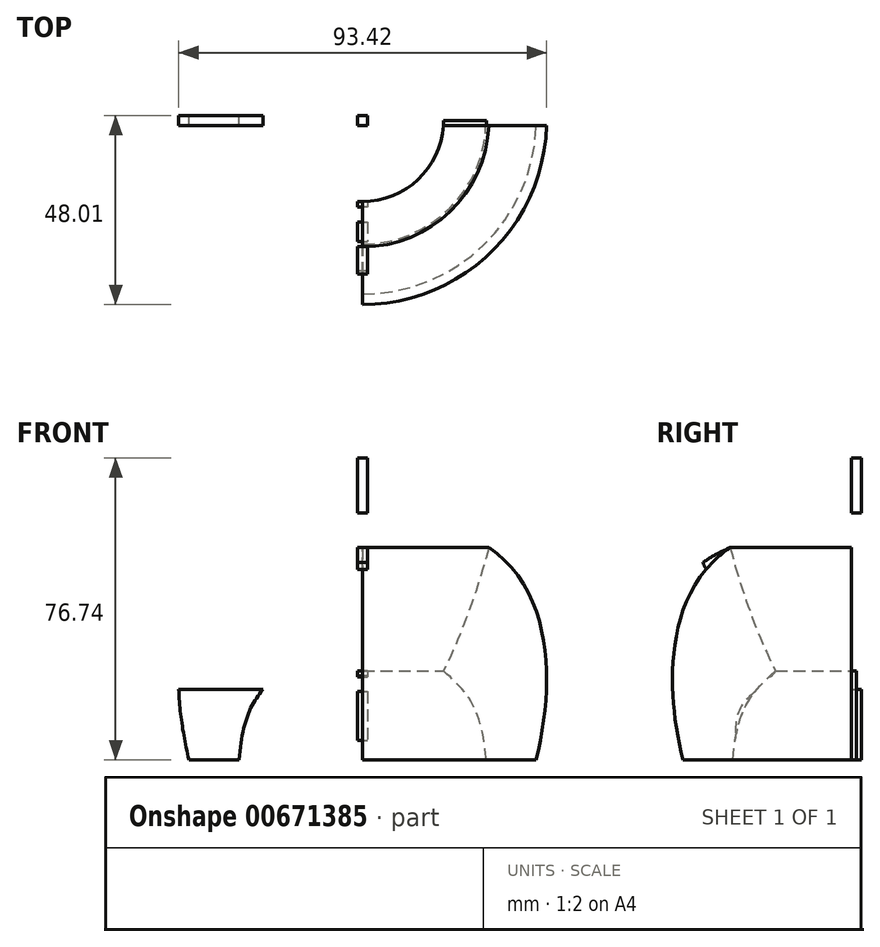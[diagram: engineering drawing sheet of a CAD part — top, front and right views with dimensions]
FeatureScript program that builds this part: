
annotation { "Feature Type Name" : "Feature", "Feature Type Description" : "" }
export const myFeature = defineFeature(function(context is Context, id is Id, definition is map)
    precondition{}
    {
        {
            var Q0;
            Q0=qCreatedBy(makeId("Front.planeOp"),FACE);
            var sketch = newSketch(context, id + "F0", { "sketchPlane" : qUnion([Q0])});
            skLineSegment(sketch, "E0", {"start": v(0, 0) * mm, "end": v(0, 203.2) * mm, "construction": true});
            skFitSpline(sketch, "E1", {"points": [v(0, 203.2) * mm, v(38.56, 109.4) * mm, v(12.7, 9.52) * mm], "startDerivative": vector(125.06, -59.8) * mm, "endDerivative": vector(-79, -104.87) * mm});
            skFitSpline(sketch, "E2.MirrorCS", {"points": [v(0, 203.2) * mm, v(-38.56, 109.4) * mm, v(-12.7, 9.52) * mm], "startDerivative": vector(-125.06, -59.8) * mm, "endDerivative": vector(79, -104.87) * mm});
            skLineSegment(sketch, "E3", {"start": v(-12.7, 9.52) * mm, "end": v(12.7, 9.53) * mm});
            skLineSegment(sketch, "E4", {"start": v(31.41, 0) * mm, "end": v(44.11, 0) * mm});
            skFitSpline(sketch, "E5", {"points": [v(44.11, 0) * mm, v(46.52, 25.68) * mm, v(32.09, 54) * mm], "startDerivative": vector(12.74, 54.23) * mm, "endDerivative": vector(-60.54, 42.84) * mm});
            skFitSpline(sketch, "E6", {"points": [v(31.41, 0) * mm, v(20.56, 22.58) * mm], "startDerivative": vector(-3.27, 36.67) * mm, "endDerivative": vector(-20.85, 17.87) * mm});
            skFitSpline(sketch, "E7.MirrorCS", {"points": [v(-44.11, 0) * mm, v(-46.52, 25.68) * mm, v(-32.09, 54) * mm], "startDerivative": vector(-12.74, 54.23) * mm, "endDerivative": vector(60.54, 42.84) * mm});
            skLineSegment(sketch, "E8.MirrorCS", {"start": v(-31.41, 0) * mm, "end": v(-44.11, 0) * mm});
            skFitSpline(sketch, "E9.MirrorCS", {"points": [v(-31.41, 0) * mm, v(-20.56, 22.58) * mm], "startDerivative": vector(3.27, 36.67) * mm, "endDerivative": vector(20.85, 17.87) * mm});
            skSolve(sketch);
        }
        {
            var Q0;
            {var subQ4=sQuery(id+"F0.wireOp",EDGE,"E3");Q0=makeQuery(id+"F0.imprint","IMPRINT",FACE,{"disambiguationData":[TD([[makeQuery(id+"F0.imprint","IMPRINT",EDGE,{"derivedFrom":subQ4}),1.0]])]});}
            var Q1;
            {var subQ0=sQuery(id+"F0.wireOp",EDGE,"E7.MirrorCS");Q1=makeQuery(id+"F0.imprint","IMPRINT",FACE,{"disambiguationData":[TD([[makeQuery(id+"F0.imprint","IMPRINT",EDGE,{"derivedFrom":subQ0}),-1.0]])]});}
            var Q2;
            Q2=makeQuery(id+"F0.imprint","IMPRINT",FACE,{"disambiguationData":[TD([[makeQuery(id+"F0.imprint","IMPRINT",EDGE,{"derivedFrom":sQuery(id+"F0.wireOp",EDGE,"E4")}),1.0]])]});
            extrude(context, id + "F1", {"entities" : qUnion([Q0, Q1, Q2]), "endBound" : BoundingType.SYMMETRIC, "depth" : 2.54 * mm, "offsetDistance" : 25.4 * mm});
        }
        {
            var Q0;
            Q0=makeQuery(id+"F1.opExtrude","SWEPT_EDGE",EDGE,{"disambiguationData":[OSD([sQuery(id+"F0.wireOp",EDGE,"E1"),sQuery(id+"F0.wireOp",EDGE,"E2.MirrorCS")])]});
            fillet(context, id + "F2", {"entities" : qUnion([Q0]), "radius" : 12.7 * mm, "tangentPropagation" : true, "allowEdgeOverflow" : false});
        }
        {
            var Q0;
            Q0=makeQuery(id+"F0.imprint","IMPRINT",FACE,{"disambiguationData":[TD([[makeQuery(id+"F0.imprint","IMPRINT",EDGE,{"derivedFrom":sQuery(id+"F0.wireOp",EDGE,"E4")}),1.0]])]});
            var Q1;
            Q1=sQuery(id+"F0.wireOp",EDGE,"E0");
            revolve(context, id + "F3", {"entities" : qUnion([Q0]), "axis" : qUnion([Q1]), "revolveType" : RevolveType.ONE_DIRECTION, "oppositeDirection" : true, "angle" : 90 * degree});
        }
        {
            var Q0;
            Q0=makeQuery(id+"F3.opRevolve","CAP_FACE",FACE,{"disambiguationData":[OSD([sQuery(id+"F0.wireOp",EDGE,"E1"),sQuery(id+"F0.wireOp",EDGE,"E4"),sQuery(id+"F0.wireOp",EDGE,"E5"),sQuery(id+"F0.wireOp",EDGE,"E6")])],"isStart":false});
            var sketch = newSketch(context, id + "F4", { "sketchPlane" : qUnion([Q0])});
            skFitSpline(sketch, "E10.0.0", {"points": [v(20.56, 22.58) * mm, v(23.55, 19.29) * mm, v(29.71, 12.74) * mm, v(30.83, 4.2) * mm, v(31.41, 0) * mm]});
            skLineSegment(sketch, "E10.0.1", {"start": v(31.41, 0) * mm, "end": v(44.11, 0) * mm});
            skFitSpline(sketch, "E10.0.2", {"points": [v(44.11, 0) * mm, v(46.12, 8.57) * mm, v(48.46, 25.8) * mm, v(42.7, 46.48) * mm, v(32.09, 54) * mm]});
            skFitSpline(sketch, "E10.0.3", {"points": [v(0, 203.2) * mm, v(20.75, 193.28) * mm, v(53.81, 107.91) * mm, v(25.92, 27.08) * mm, v(12.7, 9.52) * mm]});
            skFitSpline(sketch, "E11.MirrorCS", {"points": [v(-44.11, 0) * mm, v(-46.12, 8.57) * mm, v(-48.46, 25.8) * mm, v(-42.7, 46.48) * mm, v(-32.09, 54) * mm]});
            skLineSegment(sketch, "E12.MirrorCS", {"start": v(-31.41, 0) * mm, "end": v(-44.11, 0) * mm});
            skFitSpline(sketch, "E13.MirrorCS", {"points": [v(-20.56, 22.58) * mm, v(-23.55, 19.29) * mm, v(-29.71, 12.74) * mm, v(-30.83, 4.2) * mm, v(-31.41, 0) * mm]});
            skLineSegment(sketch, "E14", {"start": v(0, 62.78) * mm, "end": v(-20.26, 62.78) * mm, "construction": true});
            skFitSpline(sketch, "E15", {"points": [v(0, 62.78) * mm, v(32.09, 54) * mm], "startDerivative": vector(35.76, 0) * mm, "endDerivative": vector(29.19, -20.66) * mm});
            skLineSegment(sketch, "E16", {"start": v(0, 30.67) * mm, "end": v(-16.56, 30.67) * mm, "construction": true});
            skFitSpline(sketch, "E17", {"points": [v(0, 30.67) * mm, v(20.56, 22.58) * mm], "startDerivative": vector(22.33, 0) * mm, "endDerivative": vector(16.96, -14.53) * mm});
            skFitSpline(sketch, "E18.MirrorCS", {"points": [v(0, 62.78) * mm, v(-32.09, 54) * mm], "startDerivative": vector(-35.76, 0) * mm, "endDerivative": vector(-29.19, -20.66) * mm});
            skFitSpline(sketch, "E19.MirrorCS", {"points": [v(0, 30.67) * mm, v(-20.56, 22.58) * mm], "startDerivative": vector(-22.33, 0) * mm, "endDerivative": vector(-16.96, -14.53) * mm});
            skSolve(sketch);
        }
        {
            var Q0;
            Q0=makeQuery(id+"F4.imprint","IMPRINT",FACE,{"disambiguationData":[TD([[makeQuery(id+"F4.imprint","IMPRINT",EDGE,{"derivedFrom":sQuery(id+"F4.wireOp",EDGE,"E10.0.3")}),-1.0]])]});
            var Q1;
            Q1=makeQuery(id+"F4.imprint","IMPRINT",FACE,{"disambiguationData":[TD([[makeQuery(id+"F4.imprint","IMPRINT",EDGE,{"derivedFrom":sQuery(id+"F4.wireOp",EDGE,"E10.0.0")}),-1.0]])]});
            extrude(context, id + "F5", {"entities" : qUnion([Q0, Q1]), "endBound" : BoundingType.SYMMETRIC, "depth" : 2.54 * mm, "offsetDistance" : 25.4 * mm});
        }
        {
            var Q0;
            Q0=makeQuery(id+"F5.opExtrude","CAP_FACE",FACE,{"disambiguationData":[OSD([sQuery(id+"F4.wireOp",EDGE,"E10.0.0"),sQuery(id+"F4.wireOp",EDGE,"E10.0.1"),sQuery(id+"F4.wireOp",EDGE,"E10.0.2"),sQuery(id+"F4.wireOp",EDGE,"E11.MirrorCS"),sQuery(id+"F4.wireOp",EDGE,"E12.MirrorCS"),sQuery(id+"F4.wireOp",EDGE,"E13.MirrorCS"),sQuery(id+"F4.wireOp",EDGE,"E15"),sQuery(id+"F4.wireOp",EDGE,"E17"),sQuery(id+"F4.wireOp",EDGE,"E18.MirrorCS"),sQuery(id+"F4.wireOp",EDGE,"E19.MirrorCS")])],"isStart":true});
            var sketch = newSketch(context, id + "F6", { "sketchPlane" : qUnion([Q0])});
            skLineSegment(sketch, "E20.bottom", {"start": v(1.27, 43.37) * mm, "end": v(-1.27, 43.37) * mm});
            skLineSegment(sketch, "E20.top", {"start": v(1.27, 17.97) * mm, "end": v(-1.27, 17.97) * mm});
            skLineSegment(sketch, "E20.left", {"start": v(1.27, 43.37) * mm, "end": v(1.27, 17.97) * mm});
            skLineSegment(sketch, "E20.right", {"start": v(-1.27, 43.37) * mm, "end": v(-1.27, 17.97) * mm});
            skPoint(sketch, "E20.middle", {"position": v(0, 30.67) * mm});
            skSolve(sketch);
        }
        {
            var Q0;
            {var subQ1=sQuery(id+"F6.wireOp",EDGE,"E20.bottom");Q0=makeQuery(id+"F6.imprint","IMPRINT",FACE,{"disambiguationData":[TD([[makeQuery(id+"F6.imprint","IMPRINT",EDGE,{"derivedFrom":subQ1}),1.0]])]});}
            var Q1;
            {var subQ5=sQuery(id+"F6.wireOp",EDGE,"E20.top");Q1=makeQuery(id+"F6.imprint","IMPRINT",FACE,{"disambiguationData":[TD([[makeQuery(id+"F6.imprint","IMPRINT",EDGE,{"derivedFrom":subQ5}),-1.0]])]});}
            extrude(context, id + "F7", {"entities" : qUnion([Q0, Q1]), "operationType" : NewBodyOperationType.REMOVE, "endBound" : BoundingType.THROUGH_ALL, "oppositeDirection" : true, "depth" : 25.4 * mm, "offsetDistance" : 25.4 * mm});
        }
        {
            var Q0;
            Q0=makeQuery(id+"F5.opExtrude","SWEPT_BODY",BODY,{"disambiguationData":[OSD([sQuery(id+"F4.wireOp",EDGE,"E10.0.0"),sQuery(id+"F4.wireOp",EDGE,"E10.0.1"),sQuery(id+"F4.wireOp",EDGE,"E10.0.2"),sQuery(id+"F4.wireOp",EDGE,"E11.MirrorCS"),sQuery(id+"F4.wireOp",EDGE,"E12.MirrorCS"),sQuery(id+"F4.wireOp",EDGE,"E13.MirrorCS"),sQuery(id+"F4.wireOp",EDGE,"E15"),sQuery(id+"F4.wireOp",EDGE,"E17"),sQuery(id+"F4.wireOp",EDGE,"E18.MirrorCS"),sQuery(id+"F4.wireOp",EDGE,"E19.MirrorCS")])]});
            var Q1;
            Q1=makeQuery(id+"F1.opExtrude","SWEPT_BODY",BODY,{"disambiguationData":[OSD([sQuery(id+"F0.wireOp",EDGE,"E1"),sQuery(id+"F0.wireOp",EDGE,"E2.MirrorCS"),sQuery(id+"F0.wireOp",EDGE,"E3"),sQuery(id+"F0.wireOp",EDGE,"E4"),sQuery(id+"F0.wireOp",EDGE,"E5"),sQuery(id+"F0.wireOp",EDGE,"E6"),sQuery(id+"F0.wireOp",EDGE,"E7.MirrorCS"),sQuery(id+"F0.wireOp",EDGE,"E8.MirrorCS"),sQuery(id+"F0.wireOp",EDGE,"E9.MirrorCS")])]});
            booleanBodies(context, id + "F8", {"operationType" : BooleanOperationType.SUBTRACTION, "tools" : qUnion([Q0]), "targets" : qUnion([Q1]), "keepTools" : true});
        }
        {
            var Q0;
            Q0=makeQuery(id+"F1.opExtrude","CAP_FACE",FACE,{"disambiguationData":[OSD([sQuery(id+"F0.wireOp",EDGE,"E1"),sQuery(id+"F0.wireOp",EDGE,"E2.MirrorCS"),sQuery(id+"F0.wireOp",EDGE,"E3"),sQuery(id+"F0.wireOp",EDGE,"E4"),sQuery(id+"F0.wireOp",EDGE,"E5"),sQuery(id+"F0.wireOp",EDGE,"E6"),sQuery(id+"F0.wireOp",EDGE,"E7.MirrorCS"),sQuery(id+"F0.wireOp",EDGE,"E8.MirrorCS"),sQuery(id+"F0.wireOp",EDGE,"E9.MirrorCS")])],"isStart":false});
            var sketch = newSketch(context, id + "F9", { "sketchPlane" : qUnion([Q0])});
            skLineSegment(sketch, "E21.bottom", {"start": v(-1.27, 62.77) * mm, "end": v(1.27, 62.77) * mm});
            skLineSegment(sketch, "E21.top", {"start": v(-1.27, 76.74) * mm, "end": v(1.27, 76.74) * mm});
            skLineSegment(sketch, "E21.left", {"start": v(-1.27, 62.77) * mm, "end": v(-1.27, 76.74) * mm});
            skLineSegment(sketch, "E21.right", {"start": v(1.27, 62.77) * mm, "end": v(1.27, 76.74) * mm});
            skSolve(sketch);
        }
        {
            var Q0;
            Q0=makeQuery(id+"F9.imprint","IMPRINT",FACE,{"disambiguationData":[TD([[makeQuery(id+"F9.imprint","IMPRINT",EDGE,{"derivedFrom":sQuery(id+"F9.wireOp",EDGE,"E21.bottom")}),-1.0]])]});
            extrude(context, id + "F10", {"entities" : qUnion([Q0]), "operationType" : NewBodyOperationType.REMOVE, "endBound" : BoundingType.THROUGH_ALL, "oppositeDirection" : true, "depth" : 25.4 * mm, "offsetDistance" : 25.4 * mm});
        }
        {
            var Q0;
            Q0=makeQuery(id+"F1.opExtrude","CAP_FACE",FACE,{"disambiguationData":[OSD([sQuery(id+"F0.wireOp",EDGE,"E1"),sQuery(id+"F0.wireOp",EDGE,"E2.MirrorCS"),sQuery(id+"F0.wireOp",EDGE,"E3"),sQuery(id+"F0.wireOp",EDGE,"E4"),sQuery(id+"F0.wireOp",EDGE,"E5"),sQuery(id+"F0.wireOp",EDGE,"E6"),sQuery(id+"F0.wireOp",EDGE,"E7.MirrorCS"),sQuery(id+"F0.wireOp",EDGE,"E8.MirrorCS"),sQuery(id+"F0.wireOp",EDGE,"E9.MirrorCS")])],"isStart":true});
            var sketch = newSketch(context, id + "F11", { "sketchPlane" : qUnion([Q0])});
            skCircle(sketch, "E22", {"center": v(0, 153.4) * mm, "radius": 9.53 * mm});
            skCircle(sketch, "E23", {"center": v(0, 171.25) * mm, "radius": 5.66 * mm});
            skCircle(sketch, "E24", {"center": v(0, 182.75) * mm, "radius": 3.18 * mm});
            skLineSegment(sketch, "E25", {"start": v(-9.3, 155.47) * mm, "end": v(-3.1, 183.43) * mm, "construction": true});
            skLineSegment(sketch, "E26", {"start": v(0, 165.59) * mm, "end": v(0, 162.93) * mm, "construction": true});
            skLineSegment(sketch, "E27", {"start": v(0, 176.91) * mm, "end": v(0, 179.57) * mm, "construction": true});
            skSolve(sketch);
        }
        {
            var Q0;
            Q0 = qSketchRegion(id + "F11", true);
            extrude(context, id + "F12", {"entities" : qUnion([Q0]), "operationType" : NewBodyOperationType.REMOVE, "endBound" : BoundingType.THROUGH_ALL, "oppositeDirection" : true, "depth" : 25.4 * mm, "offsetDistance" : 25.4 * mm});
        }
    });
